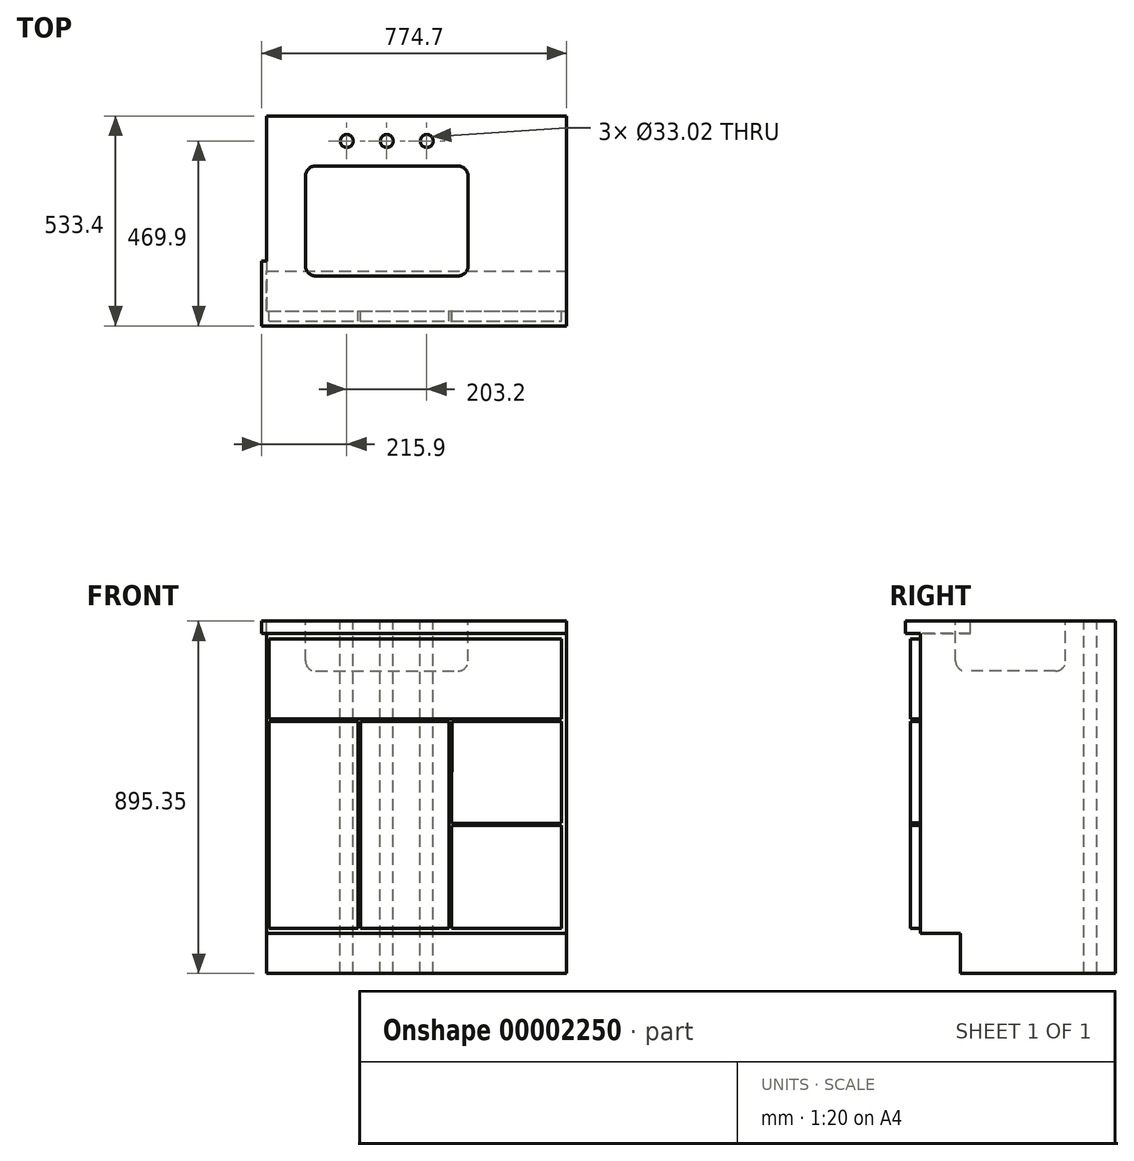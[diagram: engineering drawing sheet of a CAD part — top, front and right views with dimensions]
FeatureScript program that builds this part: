
annotation { "Feature Type Name" : "Feature", "Feature Type Description" : "" }
export const myFeature = defineFeature(function(context is Context, id is Id, definition is map)
    precondition{}
    {
        {
            var Q0;
            Q0=qCreatedBy(makeId("Right.planeOp"),FACE);
            var sketch = newSketch(context, id + "F0", { "sketchPlane" : qUnion([Q0])});
            skLineSegment(sketch, "E0.bottom", {"start": v(0, 0) * mm, "end": v(-393.7, 0) * mm});
            skLineSegment(sketch, "E0.left", {"start": v(0, 0) * mm, "end": v(0, 895.35) * mm});
            skLineSegment(sketch, "E0.right", {"start": v(-495.3, 101.6) * mm, "end": v(-495.3, 863.6) * mm});
            skLineSegment(sketch, "E1.top", {"start": v(-495.3, 101.6) * mm, "end": v(-393.7, 101.6) * mm});
            skLineSegment(sketch, "E1.right", {"start": v(-393.7, 0) * mm, "end": v(-393.7, 101.6) * mm});
            skLineSegment(sketch, "E2.bottom", {"start": v(-495.3, 863.6) * mm, "end": v(-533.4, 863.6) * mm});
            skLineSegment(sketch, "E2.top", {"start": v(0, 895.35) * mm, "end": v(-533.4, 895.35) * mm});
            skLineSegment(sketch, "E2.right", {"start": v(-533.4, 863.6) * mm, "end": v(-533.4, 895.35) * mm});
            skSolve(sketch);
        }
        {
            var Q0;
            Q0=makeQuery(id+"F0.imprint","IMPRINT",FACE,{"disambiguationData":[TD([[makeQuery(id+"F0.imprint","IMPRINT",EDGE,{"derivedFrom":sQuery(id+"F0.wireOp",EDGE,"E0.bottom")}),-1.0]])]});
            extrude(context, id + "F1", {"entities" : qUnion([Q0]), "oppositeDirection" : true, "depth" : 762 * mm});
        }
        {
            var Q0;
            Q0=makeQuery(id+"F1.opExtrude","SWEPT_FACE",FACE,{"disambiguationData":[OSD([sQuery(id+"F0.wireOp",EDGE,"E0.right")])]});
            var sketch = newSketch(context, id + "F2", { "sketchPlane" : qUnion([Q0])});
            skLineSegment(sketch, "E3.0", {"start": v(-12.7, 114.32) * mm, "end": v(-12.7, 376.28) * mm});
            skLineSegment(sketch, "E4", {"start": v(-292.1, 381.4) * mm, "end": v(-12.7, 382.63) * mm});
            skLineSegment(sketch, "E5.0", {"start": v(-292.08, 639.97) * mm, "end": v(-12.7, 639.97) * mm});
            skLineSegment(sketch, "E6.0", {"start": v(-292.1, 375.04) * mm, "end": v(-12.7, 376.28) * mm});
            skLineSegment(sketch, "E7.0", {"start": v(-755.65, 849.52) * mm, "end": v(-755.65, 646.32) * mm});
            skLineSegment(sketch, "E8", {"start": v(-755.65, 646.32) * mm, "end": v(-12.7, 646.32) * mm});
            skLineSegment(sketch, "E9", {"start": v(-755.65, 639.97) * mm, "end": v(-530.23, 639.97) * mm});
            skLineSegment(sketch, "E10", {"start": v(-530.23, 639.97) * mm, "end": v(-530.23, 114.32) * mm});
            skLineSegment(sketch, "E11.0", {"start": v(-523.88, 639.97) * mm, "end": v(-523.88, 114.32) * mm});
            skLineSegment(sketch, "E12.trimOffspring", {"start": v(-755.65, 639.97) * mm, "end": v(-755.65, 114.32) * mm});
            skLineSegment(sketch, "E13.trimOffspring", {"start": v(-523.88, 639.97) * mm, "end": v(-298.45, 639.97) * mm});
            skLineSegment(sketch, "E14.trimOffspring", {"start": v(-755.65, 114.32) * mm, "end": v(-530.23, 114.32) * mm});
            skLineSegment(sketch, "E15.trimOffspring", {"start": v(-523.88, 114.32) * mm, "end": v(-298.45, 114.32) * mm});
            skLineSegment(sketch, "E16.trimOffspring", {"start": v(-292.1, 375.04) * mm, "end": v(-292.11, 114.32) * mm});
            skLineSegment(sketch, "E17.trimOffspring", {"start": v(-292.08, 639.97) * mm, "end": v(-292.1, 381.4) * mm});
            skLineSegment(sketch, "E18.trimOffspring", {"start": v(-298.45, 639.97) * mm, "end": v(-298.45, 114.32) * mm});
            skLineSegment(sketch, "E19.trimOffspring", {"start": v(-12.7, 646.32) * mm, "end": v(-12.7, 849.52) * mm});
            skLineSegment(sketch, "E20.trimOffspring", {"start": v(-12.7, 382.63) * mm, "end": v(-12.7, 639.97) * mm});
            skLineSegment(sketch, "E21.trimOffspring", {"start": v(-755.65, 849.52) * mm, "end": v(-12.7, 849.52) * mm});
            skLineSegment(sketch, "E22.trimOffspring", {"start": v(-292.11, 114.32) * mm, "end": v(-12.7, 114.32) * mm});
            skSolve(sketch);
        }
        {
            var Q0;
            Q0=makeQuery(id+"F2.imprint","IMPRINT",FACE,{"disambiguationData":[TD([[makeQuery(id+"F2.imprint","IMPRINT",EDGE,{"derivedFrom":sQuery(id+"F2.wireOp",EDGE,"E3.3")}),-1.0]])]});
            var Q1;
            Q1=makeQuery(id+"F2.imprint","IMPRINT",FACE,{"disambiguationData":[TD([[makeQuery(id+"F2.imprint","IMPRINT",EDGE,{"derivedFrom":sQuery(id+"F2.wireOp",EDGE,"b5957af1-2dda-447e-bfd9-5532a77e66a5.0")}),-1.0]])]});
            var Q2;
            Q2=makeQuery(id+"F2.imprint","IMPRINT",FACE,{"disambiguationData":[TD([[makeQuery(id+"F2.imprint","IMPRINT",EDGE,{"derivedFrom":sQuery(id+"F2.wireOp",EDGE,"d213ee8b-bd27-44e1-98d4-293f2c210446")}),1.0]])]});
            var Q3;
            Q3=makeQuery(id+"F2.imprint","IMPRINT",FACE,{"disambiguationData":[TD([[makeQuery(id+"F2.imprint","IMPRINT",EDGE,{"derivedFrom":sQuery(id+"F2.wireOp",EDGE,"E4")}),1.0]])]});
            var Q4;
            Q4=makeQuery(id+"F2.imprint","IMPRINT",FACE,{"disambiguationData":[TD([[makeQuery(id+"F2.imprint","IMPRINT",EDGE,{"derivedFrom":sQuery(id+"F2.wireOp",EDGE,"E11.0")}),1.0]])]});
            var Q5;
            Q5=makeQuery(id+"F2.imprint","IMPRINT",FACE,{"disambiguationData":[TD([[makeQuery(id+"F2.imprint","IMPRINT",EDGE,{"derivedFrom":sQuery(id+"F2.wireOp",EDGE,"E9")}),-1.0]])]});
            var Q6;
            Q6=makeQuery(id+"F2.imprint","IMPRINT",FACE,{"disambiguationData":[TD([[makeQuery(id+"F2.imprint","IMPRINT",EDGE,{"derivedFrom":sQuery(id+"F2.wireOp",EDGE,"E3.0")}),1.0]])]});
            var Q7;
            Q7=makeQuery(id+"F2.imprint","IMPRINT",FACE,{"disambiguationData":[TD([[makeQuery(id+"F2.imprint","IMPRINT",EDGE,{"derivedFrom":sQuery(id+"F2.wireOp",EDGE,"E3.1")}),1.0]])]});
            var Q8;
            Q8=makeQuery(id+"F2.imprint","IMPRINT",FACE,{"disambiguationData":[TD([[makeQuery(id+"F2.imprint","IMPRINT",EDGE,{"derivedFrom":sQuery(id+"F2.wireOp",EDGE,"94968935-6469-4bd7-b6ec-2cd1eeb32554")}),1.0]])]});
            var Q9;
            Q9=makeQuery(id+"F2.imprint","IMPRINT",FACE,{"disambiguationData":[TD([[makeQuery(id+"F2.imprint","IMPRINT",EDGE,{"derivedFrom":sQuery(id+"F2.wireOp",EDGE,"E7.0")}),1.0]])]});
            extrude(context, id + "F3", {"entities" : qUnion([Q0, Q1, Q2, Q3, Q4, Q5, Q6, Q7, Q8, Q9]), "operationType" : NewBodyOperationType.ADD, "depth" : 25.4 * mm});
        }
        {
            var Q0;
            Q0=makeQuery(id+"F1.opExtrude","SWEPT_FACE",FACE,{"disambiguationData":[OSD([sQuery(id+"F0.wireOp",EDGE,"E2.top")])]});
            var sketch = newSketch(context, id + "F4", { "sketchPlane" : qUnion([Q0])});
            skLineSegment(sketch, "E23.bottom", {"start": v(-638.18, -127) * mm, "end": v(-276.23, -127) * mm});
            skLineSegment(sketch, "E23.top", {"start": v(-638.18, -406.4) * mm, "end": v(-276.23, -406.4) * mm});
            skLineSegment(sketch, "E23.left", {"start": v(-663.58, -152.4) * mm, "end": v(-663.58, -381) * mm});
            skLineSegment(sketch, "E23.right", {"start": v(-250.83, -152.4) * mm, "end": v(-250.83, -381) * mm});
            skLineSegment(sketch, "E24", {"start": v(-457.2, -127) * mm, "end": v(-457.2, -406.4) * mm, "construction": true});
            skLineSegment(sketch, "E25", {"start": v(-457.2, 0) * mm, "end": v(-457.2, -127) * mm});
            skEllipse(sketch, "E26", {"center": v(-457.2, -266.7) * mm, "majorRadius": 139.7 * mm, "minorRadius": 206.38 * mm, "majorAxis": v(0, 1), "construction": true});
            skPoint(sketch, "E27.visualSharp", {"position": v(-250.83, -127) * mm});
            skArc(sketch, "E27.filletArc", {"start": v(-250.83, -152.4) * mm, "mid": v(-258.26, -134.44) * mm, "end": v(-276.23, -127) * mm});
            skPoint(sketch, "E28.visualSharp", {"position": v(-250.83, -406.4) * mm});
            skArc(sketch, "E28.filletArc", {"start": v(-276.23, -406.4) * mm, "mid": v(-258.26, -398.96) * mm, "end": v(-250.83, -381) * mm});
            skPoint(sketch, "E29.visualSharp", {"position": v(-663.58, -406.4) * mm});
            skArc(sketch, "E29.filletArc", {"start": v(-663.58, -381) * mm, "mid": v(-656.14, -398.96) * mm, "end": v(-638.18, -406.4) * mm});
            skPoint(sketch, "E30.visualSharp", {"position": v(-663.58, -127) * mm});
            skArc(sketch, "E30.filletArc", {"start": v(-638.18, -127) * mm, "mid": v(-656.14, -134.44) * mm, "end": v(-663.58, -152.4) * mm});
            skSolve(sketch);
        }
        {
            var Q0;
            Q0=makeQuery(id+"F4.imprint","IMPRINT",FACE,{"disambiguationData":[TD([[makeQuery(id+"F4.imprint","IMPRINT",EDGE,{"derivedFrom":sQuery(id+"F4.wireOp",EDGE,"E23.top")}),1.0]])]});
            var Q1;
            Q1=makeQuery(id+"F4.imprint","IMPRINT",FACE,{"disambiguationData":[TD([[makeQuery(id+"F4.imprint","IMPRINT",EDGE,{"derivedFrom":sQuery(id+"F4.wireOp",EDGE,"E26")}),1.0]])]});
            extrude(context, id + "F5", {"entities" : qUnion([Q0, Q1]), "operationType" : NewBodyOperationType.REMOVE, "oppositeDirection" : true, "depth" : 127 * mm});
        }
        {
            var Q0;
            Q0=makeQuery(id+"F1.opExtrude","SWEPT_FACE",FACE,{"disambiguationData":[OSD([sQuery(id+"F0.wireOp",EDGE,"E2.top")])]});
            var sketch = newSketch(context, id + "F6", { "sketchPlane" : qUnion([Q0])});
            skLineSegment(sketch, "E31.bottom", {"start": v(-762, -533.4) * mm, "end": v(-774.7, -533.4) * mm});
            skLineSegment(sketch, "E31.top", {"start": v(-762, -368.3) * mm, "end": v(-774.7, -368.3) * mm});
            skLineSegment(sketch, "E31.left", {"start": v(-762, -533.4) * mm, "end": v(-762, -368.3) * mm});
            skLineSegment(sketch, "E31.right", {"start": v(-774.7, -533.4) * mm, "end": v(-774.7, -368.3) * mm});
            skSolve(sketch);
        }
        {
            var Q0;
            Q0 = qSketchRegion(id + "F6", true);
            extrude(context, id + "F7", {"entities" : qUnion([Q0]), "operationType" : NewBodyOperationType.ADD, "oppositeDirection" : true, "depth" : 31.75 * mm});
        }
        {
            var Q0;
            Q0=makeQuery(id+"F7.boolean.opBoolean","MERGE",FACE,{"derivedFrom":[makeQuery(id+"F1.opExtrude","SWEPT_FACE",FACE,{"disambiguationData":[OSD([sQuery(id+"F0.wireOp",EDGE,"E2.top")])]}),makeQuery(id+"F7.opExtrude","CAP_FACE",FACE,{"disambiguationData":[OSD([sQuery(id+"F6.wireOp",EDGE,"E31.bottom"),sQuery(id+"F6.wireOp",EDGE,"E31.top"),sQuery(id+"F6.wireOp",EDGE,"E31.left"),sQuery(id+"F6.wireOp",EDGE,"E31.right")])],"isStart":true})]});
            var sketch = newSketch(context, id + "F8", { "sketchPlane" : qUnion([Q0])});
            skCircle(sketch, "E32", {"center": v(-457.2, -63.5) * mm, "radius": 16.5 * mm});
            skCircle(sketch, "E33", {"center": v(-355.6, -63.5) * mm, "radius": 16.5 * mm});
            skLineSegment(sketch, "E34", {"start": v(-355.6, -63.5) * mm, "end": v(-558.8, -63.5) * mm, "construction": true});
            skCircle(sketch, "E35", {"center": v(-558.8, -63.5) * mm, "radius": 16.5 * mm});
            skLineSegment(sketch, "E36", {"start": v(-457.2, -127) * mm, "end": v(-457.2, -63.5) * mm, "construction": true});
            skLineSegment(sketch, "E37", {"start": v(-457.2, -127) * mm, "end": v(-457.2, 0) * mm, "construction": true});
            skSolve(sketch);
        }
        {
            var Q0;
            Q0 = qSketchRegion(id + "F8", true);
            extrude(context, id + "F9", {"entities" : qUnion([Q0]), "operationType" : NewBodyOperationType.REMOVE, "oppositeDirection" : true, "depth" : 914.4 * mm});
        }
        {
            var Q0;
            Q0=makeQuery(id+"F5.boolean.opBoolean","COPY",EDGE,{"derivedFrom":makeQuery(id+"F5.opExtrude","CAP_EDGE",EDGE,{"disambiguationData":[OSD([sQuery(id+"F4.wireOp",EDGE,"E23.bottom")])],"isStart":false})});
            fillet(context, id + "F10", {"entities" : qUnion([Q0]), "radius" : 25.4 * mm, "tangentPropagation" : true, "allowEdgeOverflow" : false});
        }
    });
